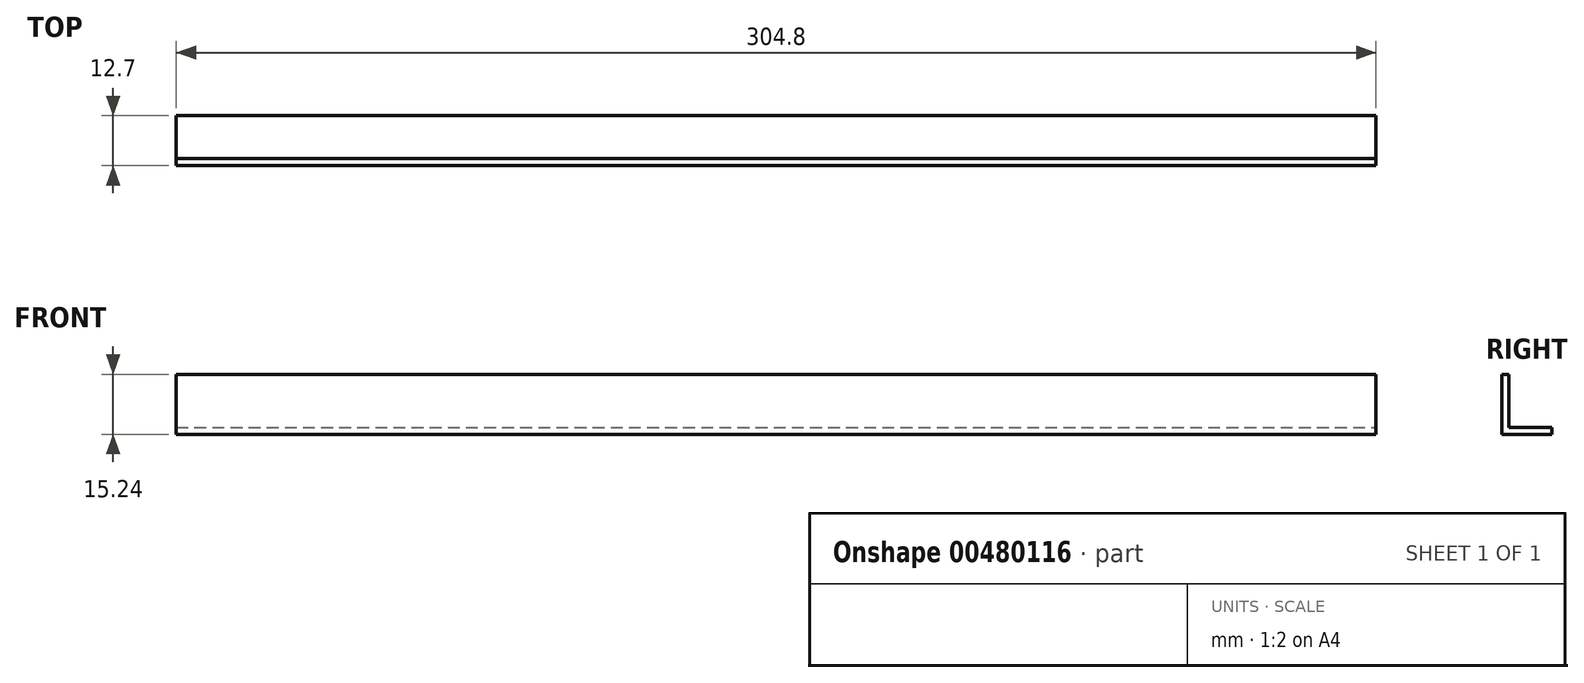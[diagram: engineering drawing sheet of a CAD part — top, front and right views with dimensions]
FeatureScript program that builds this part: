
annotation { "Feature Type Name" : "Feature", "Feature Type Description" : "" }
export const myFeature = defineFeature(function(context is Context, id is Id, definition is map)
    precondition{}
    {
        {
            var Q0;
            Q0=qCreatedBy(makeId("Right.planeOp"),FACE);
            var sketch = newSketch(context, id + "F0", { "sketchPlane" : qUnion([Q0])});
            skLineSegment(sketch, "E0", {"start": v(0, 0) * mm, "end": v(0, 15.24) * mm});
            skLineSegment(sketch, "E1", {"start": v(0, 0) * mm, "end": v(12.7, 0) * mm});
            skLineSegment(sketch, "E2", {"start": v(0, 15.24) * mm, "end": v(1.78, 15.24) * mm});
            skLineSegment(sketch, "E3", {"start": v(1.78, 15.24) * mm, "end": v(1.78, 1.78) * mm});
            skLineSegment(sketch, "E4", {"start": v(1.78, 1.78) * mm, "end": v(12.7, 1.78) * mm});
            skLineSegment(sketch, "E5", {"start": v(12.7, 1.78) * mm, "end": v(12.7, 0) * mm});
            skSolve(sketch);
        }
        {
            var Q0;
            Q0 = qSketchRegion(id + "F0", true);
            extrude(context, id + "F1", {"entities" : qUnion([Q0]), "oppositeDirection" : true, "depth" : 304.8 * mm});
        }
    });
